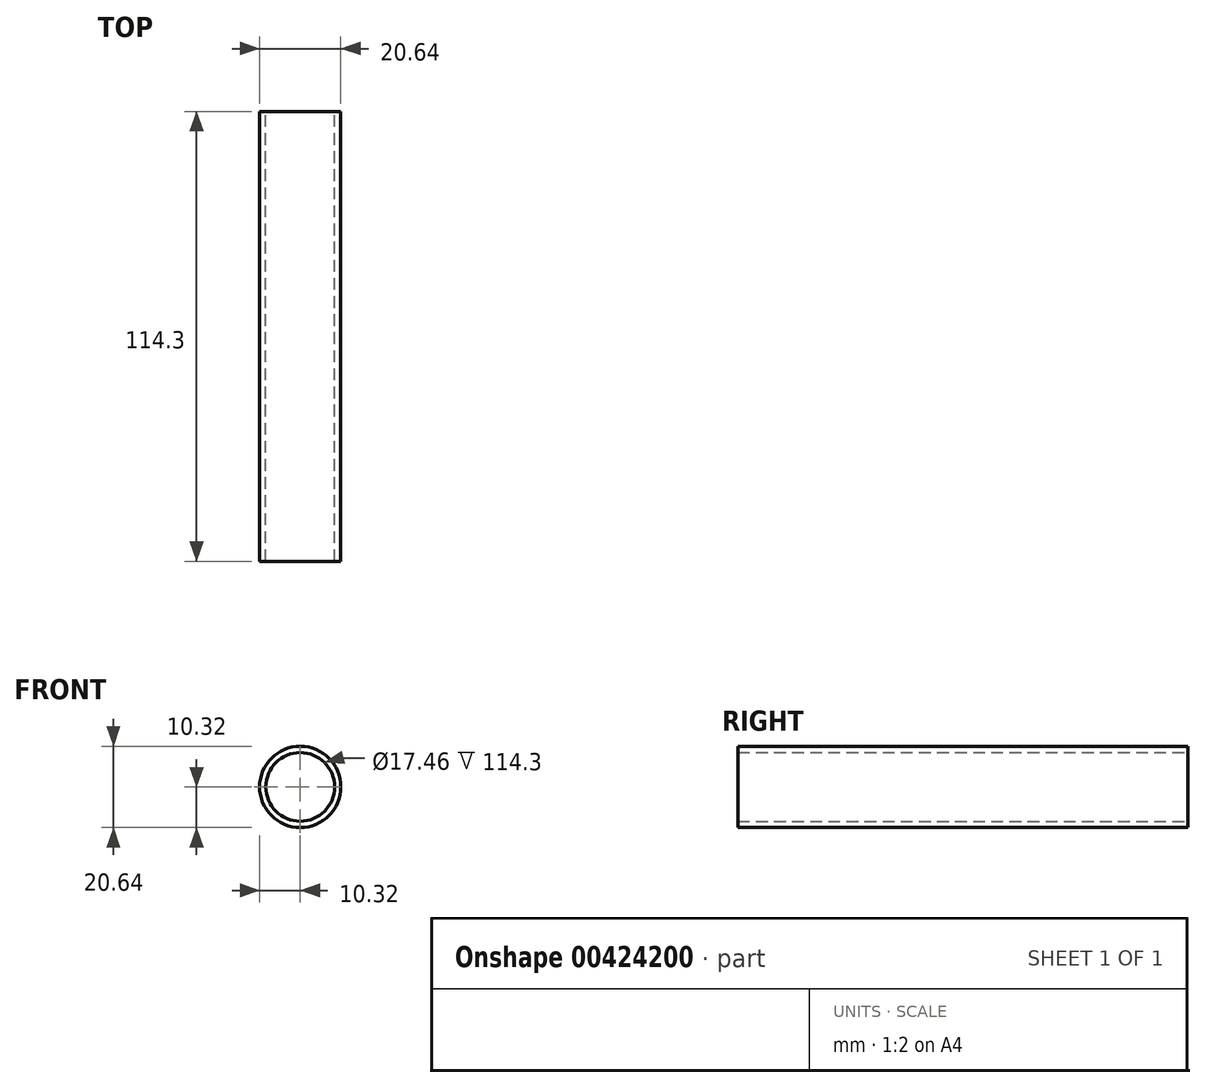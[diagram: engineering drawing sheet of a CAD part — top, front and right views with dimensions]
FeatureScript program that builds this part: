
annotation { "Feature Type Name" : "Feature", "Feature Type Description" : "" }
export const myFeature = defineFeature(function(context is Context, id is Id, definition is map)
    precondition{}
    {
        {
            var Q0;
            Q0=qCreatedBy(makeId("Front.planeOp"),FACE);
            var sketch = newSketch(context, id + "F0", { "sketchPlane" : qUnion([Q0])});
            skCircle(sketch, "E0", {"center": v(0, 0) * mm, "radius": 10.32 * mm});
            skCircle(sketch, "E1", {"center": v(0, 0) * mm, "radius": 8.73 * mm});
            skSolve(sketch);
        }
        {
            var Q0;
            Q0=makeQuery(id+"F0.imprint","IMPRINT",FACE,{"disambiguationData":[TD([[makeQuery(id+"F0.imprint","IMPRINT",EDGE,{"derivedFrom":sQuery(id+"F0.wireOp",EDGE,"E0")}),1.0]])]});
            extrude(context, id + "F1", {"entities" : qUnion([Q0]), "depth" : 114.3 * mm});
        }
    });
